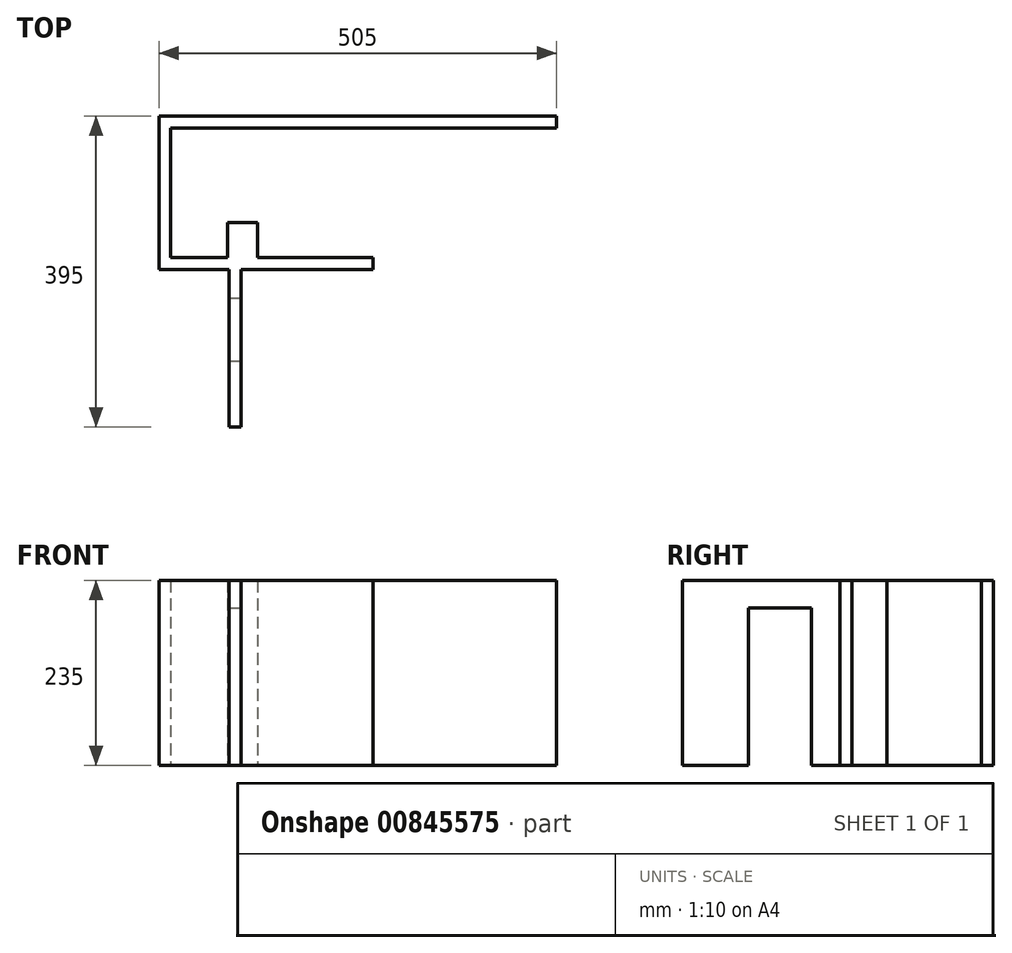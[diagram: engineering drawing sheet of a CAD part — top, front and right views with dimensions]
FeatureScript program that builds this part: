
annotation { "Feature Type Name" : "Feature", "Feature Type Description" : "" }
export const myFeature = defineFeature(function(context is Context, id is Id, definition is map)
    precondition{}
    {
        {
            var Q0;
            Q0=qCreatedBy(makeId("Top.planeOp"),FACE);
            var sketch = newSketch(context, id + "F0", { "sketchPlane" : qUnion([Q0])});
            skLineSegment(sketch, "E0", {"start": v(372.59, 188.05) * mm, "end": v(-117.41, 188.05) * mm});
            skLineSegment(sketch, "E1", {"start": v(-117.41, 188.05) * mm, "end": v(-117.41, 23.05) * mm});
            skLineSegment(sketch, "E2", {"start": v(-7.41, 23.05) * mm, "end": v(-7.41, 68.05) * mm});
            skLineSegment(sketch, "E3", {"start": v(-45.41, 68.05) * mm, "end": v(-7.41, 68.05) * mm});
            skLineSegment(sketch, "E4", {"start": v(-45.41, 68.05) * mm, "end": v(-45.41, 23.05) * mm});
            skLineSegment(sketch, "E5", {"start": v(139.59, 23.05) * mm, "end": v(139.59, 8.05) * mm});
            skLineSegment(sketch, "E6", {"start": v(139.59, 8.05) * mm, "end": v(-28.41, 8.05) * mm});
            skLineSegment(sketch, "E7", {"start": v(-28.41, 8.05) * mm, "end": v(-28.41, -191.95) * mm});
            skLineSegment(sketch, "E8", {"start": v(-28.41, -191.95) * mm, "end": v(-43.41, -191.95) * mm});
            skLineSegment(sketch, "E9", {"start": v(-43.41, -191.95) * mm, "end": v(-43.41, 8.05) * mm});
            skLineSegment(sketch, "E10", {"start": v(-43.41, 8.05) * mm, "end": v(-132.41, 8.05) * mm});
            skLineSegment(sketch, "E11", {"start": v(-132.41, 8.05) * mm, "end": v(-132.41, 203.05) * mm});
            skLineSegment(sketch, "E12", {"start": v(-132.41, 203.05) * mm, "end": v(372.59, 203.05) * mm});
            skLineSegment(sketch, "E13", {"start": v(372.59, 203.05) * mm, "end": v(372.59, 188.05) * mm});
            skLineSegment(sketch, "E14", {"start": v(-7.41, 23.05) * mm, "end": v(139.59, 23.05) * mm});
            skLineSegment(sketch, "E15", {"start": v(-45.41, 23.05) * mm, "end": v(-117.41, 23.05) * mm});
            skSolve(sketch);
        }
        {
            var Q0;
            Q0=makeQuery(id+"F0.imprint","IMPRINT",FACE,{"disambiguationData":[TD([[makeQuery(id+"F0.imprint","IMPRINT",EDGE,{"derivedFrom":sQuery(id+"F0.wireOp",EDGE,"E0")}),-1.0]])]});
            extrude(context, id + "F1", {"entities" : qUnion([Q0]), "depth" : 235 * mm, "offsetDistance" : 25 * mm});
        }
        {
            var Q0;
            Q0=makeQuery(id+"F1.opExtrude","SWEPT_FACE",FACE,{"disambiguationData":[OSD([sQuery(id+"F0.wireOp",EDGE,"E7")])]});
            var sketch = newSketch(context, id + "F2", { "sketchPlane" : qUnion([Q0])});
            skLineSegment(sketch, "E16.bottom", {"start": v(-27.95, 0) * mm, "end": v(-107.95, 0) * mm});
            skLineSegment(sketch, "E16.top", {"start": v(-27.95, 200) * mm, "end": v(-107.95, 200) * mm});
            skLineSegment(sketch, "E16.left", {"start": v(-27.95, 0) * mm, "end": v(-27.95, 200) * mm});
            skLineSegment(sketch, "E16.right", {"start": v(-107.95, 0) * mm, "end": v(-107.95, 200) * mm});
            skSolve(sketch);
        }
        {
            var Q0;
            Q0=makeQuery(id+"F2.imprint","IMPRINT",FACE,{"disambiguationData":[TD([[makeQuery(id+"F2.imprint","IMPRINT",EDGE,{"derivedFrom":sQuery(id+"F2.wireOp",EDGE,"E16.bottom")}),-1.0]])]});
            extrude(context, id + "F3", {"entities" : qUnion([Q0]), "operationType" : NewBodyOperationType.REMOVE, "endBound" : BoundingType.THROUGH_ALL, "oppositeDirection" : true, "depth" : 25 * mm, "offsetDistance" : 25 * mm});
        }
    });
